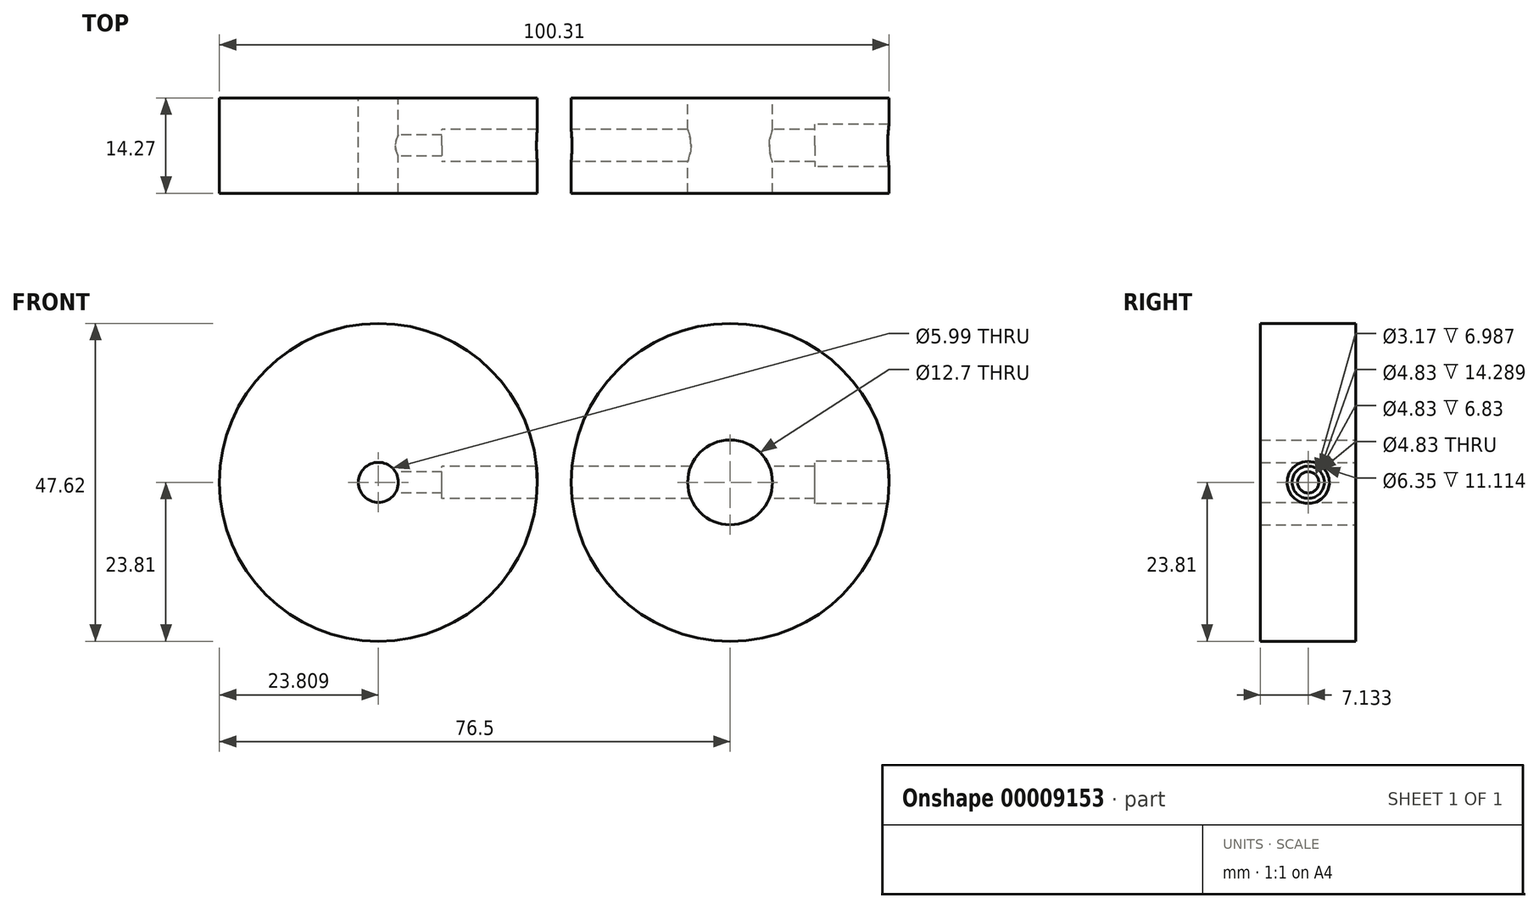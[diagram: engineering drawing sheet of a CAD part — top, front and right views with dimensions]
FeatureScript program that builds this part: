
annotation { "Feature Type Name" : "Feature", "Feature Type Description" : "" }
export const myFeature = defineFeature(function(context is Context, id is Id, definition is map)
    precondition{}
    {
        {
            var Q0;
            Q0=qCreatedBy(makeId("Front.planeOp"),FACE);
            var sketch = newSketch(context, id + "F0", { "sketchPlane" : qUnion([Q0])});
            skCircle(sketch, "E0", {"center": v(0, 0) * mm, "radius": 23.81 * mm});
            skCircle(sketch, "E1", {"center": v(0, 0) * mm, "radius": 6.35 * mm});
            skSolve(sketch);
        }
        {
            var Q0;
            Q0=makeQuery(id+"F0.imprint","IMPRINT",FACE,{"disambiguationData":[TD([[makeQuery(id+"F0.imprint","IMPRINT",EDGE,{"derivedFrom":sQuery(id+"F0.wireOp",EDGE,"E0")}),1.0]])]});
            extrude(context, id + "F1", {"entities" : qUnion([Q0]), "depth" : 14.27 * mm});
        }
        {
            var Q0;
            Q0=qCreatedBy(makeId("Front.planeOp"),FACE);
            var sketch = newSketch(context, id + "F2", { "sketchPlane" : qUnion([Q0])});
            skCircle(sketch, "E2", {"center": v(-52.7, 0) * mm, "radius": 23.81 * mm});
            skCircle(sketch, "E3", {"center": v(-52.7, 0) * mm, "radius": 3 * mm});
            skSolve(sketch);
        }
        {
            var Q0;
            Q0=makeQuery(id+"F2.imprint","IMPRINT",FACE,{"disambiguationData":[TD([[makeQuery(id+"F2.imprint","IMPRINT",EDGE,{"derivedFrom":sQuery(id+"F2.wireOp",EDGE,"E2")}),1.0]])]});
            extrude(context, id + "F3", {"entities" : qUnion([Q0]), "depth" : 14.27 * mm});
        }
        {
            var Q0;
            Q0=makeQuery(id+"F3.opExtrude","CAP_EDGE",EDGE,{"disambiguationData":[OSD([sQuery(id+"F2.wireOp",EDGE,"E2")])],"isStart":false});
            cPlane(context, id + "F4", {"entities" : qUnion([Q0]), "cplaneType" : CPlaneType.LINE_ANGLE, "offset" : 152.4 * mm, "angle" : 90 * degree, "width" : 152.4 * mm, "height" : 152.4 * mm});
        }
        {
            var Q0;
            Q0=qCreatedBy(id+"F4.planeOp",FACE);
            var sketch = newSketch(context, id + "F5", { "sketchPlane" : qUnion([Q0])});
            skLineSegment(sketch, "E4", {"start": v(0, -23.81) * mm, "end": v(-14.27, -23.81) * mm});
            skLineSegment(sketch, "E5", {"start": v(-14.27, 23.81) * mm, "end": v(0, 23.81) * mm});
            skLineSegment(sketch, "E6", {"start": v(-7.14, 23.81) * mm, "end": v(-7.14, -23.81) * mm, "construction": true});
            skCircle(sketch, "E7", {"center": v(-7.14, 0) * mm, "radius": 2.41 * mm});
            skCircle(sketch, "E8", {"center": v(-7.14, 0) * mm, "radius": 1.59 * mm});
            skSolve(sketch);
        }
        {
            var Q0;
            Q0=makeQuery(id+"F5.imprint","IMPRINT",FACE,{"disambiguationData":[TD([[makeQuery(id+"F5.imprint","IMPRINT",EDGE,{"derivedFrom":sQuery(id+"F5.wireOp",EDGE,"E8")}),1.0]])]});
            extrude(context, id + "F6", {"entities" : qUnion([Q0]), "operationType" : NewBodyOperationType.REMOVE, "endBound" : BoundingType.THROUGH_ALL, "depth" : 25.4 * mm});
        }
        {
            var Q0;
            Q0=qCreatedBy(id+"F4.planeOp",FACE);
            cPlane(context, id + "F7", {"entities" : qUnion([Q0]), "cplaneType" : CPlaneType.OFFSET, "offset" : 9.52 * mm, "width" : 152.4 * mm, "height" : 152.4 * mm});
        }
        {
            var Q0;
            Q0=qCreatedBy(id+"F7.planeOp",FACE);
            var sketch = newSketch(context, id + "F8", { "sketchPlane" : qUnion([Q0])});
            skCircle(sketch, "E9.0", {"center": v(-7.14, 0) * mm, "radius": 2.41 * mm});
            skSolve(sketch);
        }
        {
            var Q0;
            Q0=makeQuery(id+"F8.imprint","IMPRINT",FACE,{"disambiguationData":[TD([[makeQuery(id+"F8.imprint","IMPRINT",EDGE,{"derivedFrom":sQuery(id+"F8.wireOp",EDGE,"E9.0")}),1.0]])]});
            extrude(context, id + "F9", {"entities" : qUnion([Q0]), "operationType" : NewBodyOperationType.REMOVE, "endBound" : BoundingType.THROUGH_ALL, "depth" : 25.4 * mm});
        }
        {
            var Q0;
            Q0=makeQuery(id+"F1.opExtrude","CAP_EDGE",EDGE,{"disambiguationData":[OSD([sQuery(id+"F0.wireOp",EDGE,"E0")])],"isStart":false});
            cPlane(context, id + "F10", {"entities" : qUnion([Q0]), "cplaneType" : CPlaneType.LINE_ANGLE, "offset" : 152.4 * mm, "angle" : 90 * degree, "width" : 152.4 * mm, "height" : 152.4 * mm});
        }
        {
            var Q0;
            Q0=qCreatedBy(id+"F10.planeOp",FACE);
            var sketch = newSketch(context, id + "F11", { "sketchPlane" : qUnion([Q0])});
            skLineSegment(sketch, "E10", {"start": v(0, -23.81) * mm, "end": v(-14.27, -23.81) * mm});
            skLineSegment(sketch, "E11", {"start": v(-14.27, 23.81) * mm, "end": v(0, 23.81) * mm});
            skCircle(sketch, "E12", {"center": v(-7.14, 0) * mm, "radius": 2.41 * mm});
            skCircle(sketch, "E13", {"center": v(-7.14, 0) * mm, "radius": 3.18 * mm});
            skLineSegment(sketch, "E14", {"start": v(-7.14, 23.81) * mm, "end": v(-7.14, -23.81) * mm, "construction": true});
            skSolve(sketch);
        }
        {
            var Q0;
            Q0=makeQuery(id+"F11.imprint","IMPRINT",FACE,{"disambiguationData":[TD([[makeQuery(id+"F11.imprint","IMPRINT",EDGE,{"derivedFrom":sQuery(id+"F11.wireOp",EDGE,"E12")}),1.0]])]});
            extrude(context, id + "F12", {"entities" : qUnion([Q0]), "operationType" : NewBodyOperationType.REMOVE, "endBound" : BoundingType.THROUGH_ALL, "depth" : 6.35 * mm});
        }
        {
            var Q0;
            Q0=qCreatedBy(id+"F10.planeOp",FACE);
            cPlane(context, id + "F13", {"entities" : qUnion([Q0]), "cplaneType" : CPlaneType.OFFSET, "offset" : 12.7 * mm, "width" : 152.4 * mm, "height" : 152.4 * mm});
        }
        {
            var Q0;
            Q0=qCreatedBy(id+"F13.planeOp",FACE);
            var sketch = newSketch(context, id + "F14", { "sketchPlane" : qUnion([Q0])});
            skCircle(sketch, "E15.0", {"center": v(-7.14, 0) * mm, "radius": 3.18 * mm});
            skSolve(sketch);
        }
        {
            var Q0;
            Q0=makeQuery(id+"F14.imprint","IMPRINT",FACE,{"disambiguationData":[TD([[makeQuery(id+"F14.imprint","IMPRINT",EDGE,{"derivedFrom":sQuery(id+"F14.wireOp",EDGE,"E15.0")}),1.0]])]});
            extrude(context, id + "F15", {"entities" : qUnion([Q0]), "operationType" : NewBodyOperationType.REMOVE, "endBound" : BoundingType.THROUGH_ALL, "depth" : 25.4 * mm});
        }
    });
